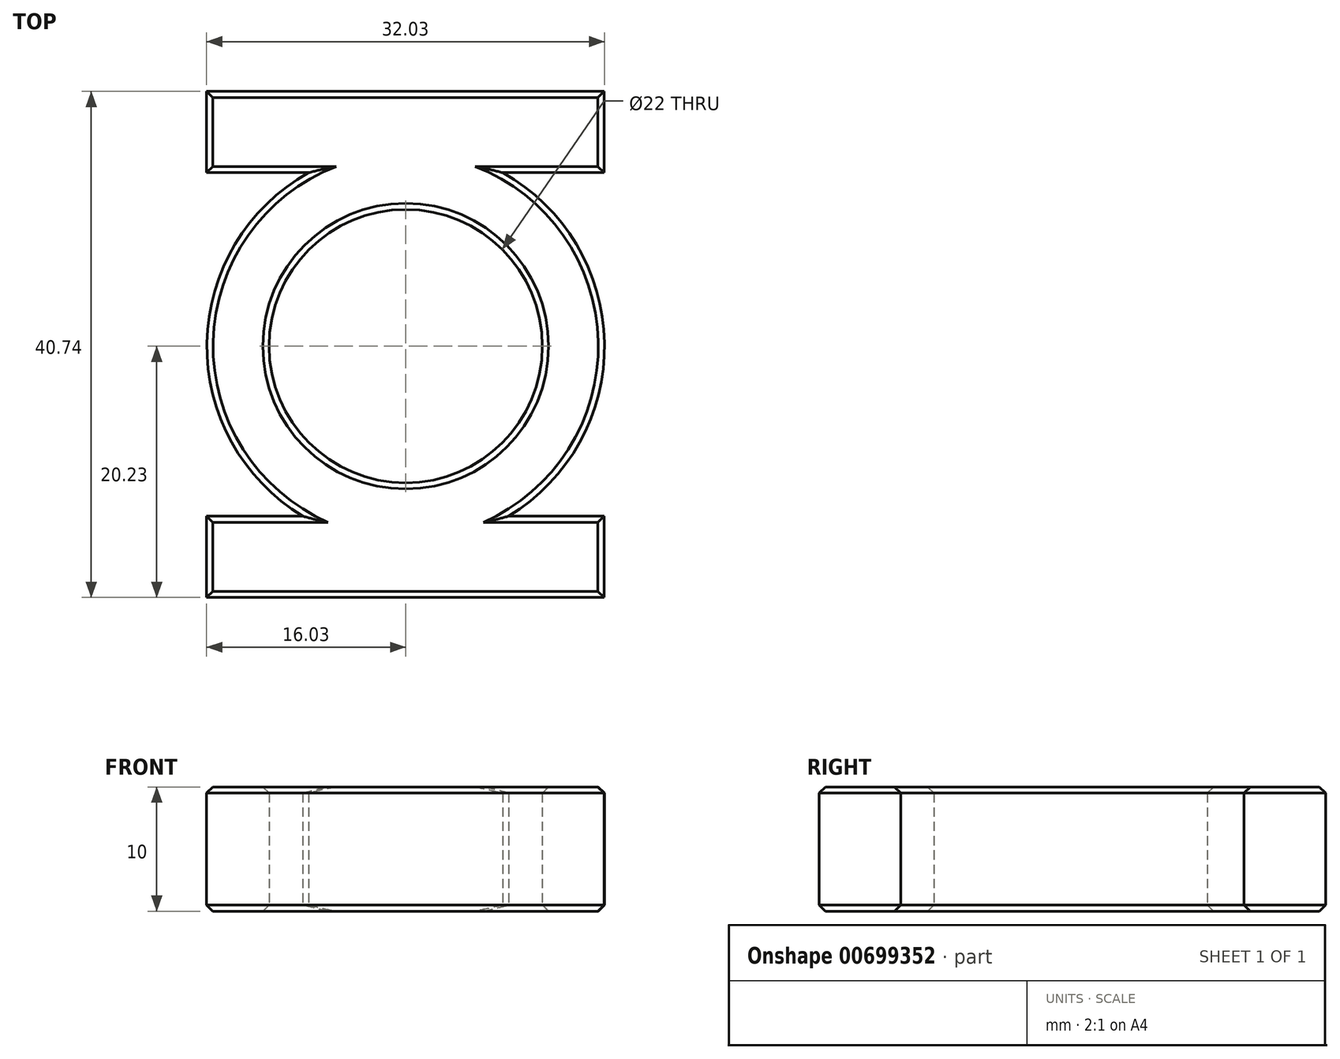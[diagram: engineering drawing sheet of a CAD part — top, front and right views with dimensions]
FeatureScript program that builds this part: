
annotation { "Feature Type Name" : "Feature", "Feature Type Description" : "" }
export const myFeature = defineFeature(function(context is Context, id is Id, definition is map)
    precondition{}
    {
        {
            var Q0;
            Q0=qCreatedBy(makeId("Top.planeOp"),FACE);
            var sketch = newSketch(context, id + "F0", { "sketchPlane" : qUnion([Q0])});
            skCircle(sketch, "E0", {"center": v(0, 0) * mm, "radius": 11 * mm});
            skArc(sketch, "E1", {"start": v(-7.82, 13.96) * mm, "mid": v(-16, 0.27) * mm, "end": v(-8.3, -13.68) * mm});
            skLineSegment(sketch, "E2", {"start": v(18.35, 0.14) * mm, "end": v(-21.03, 0.14) * mm, "construction": true});
            skLineSegment(sketch, "E3.bottom", {"start": v(-16.03, 20.5) * mm, "end": v(15.97, 20.5) * mm});
            skLineSegment(sketch, "E3.top", {"start": v(-16.03, 13.96) * mm, "end": v(-7.82, 13.96) * mm});
            skLineSegment(sketch, "E3.left", {"start": v(-16.03, 20.5) * mm, "end": v(-16.03, 13.96) * mm});
            skLineSegment(sketch, "E3.right", {"start": v(15.97, 20.5) * mm, "end": v(15.97, 13.96) * mm});
            skLineSegment(sketch, "E4.MirrorCS", {"start": v(-16.03, -20.23) * mm, "end": v(15.97, -20.23) * mm});
            skLineSegment(sketch, "E5.MirrorCS", {"start": v(15.97, -20.23) * mm, "end": v(15.97, -13.68) * mm});
            skLineSegment(sketch, "E6.MirrorCS", {"start": v(-16.03, -13.68) * mm, "end": v(-7.82, -13.68) * mm});
            skLineSegment(sketch, "E7.MirrorCS", {"start": v(-16.03, -13.68) * mm, "end": v(-8.3, -13.68) * mm});
            skLineSegment(sketch, "E8.MirrorCS", {"start": v(-16.03, -20.23) * mm, "end": v(-16.03, -13.68) * mm});
            skLineSegment(sketch, "E9", {"start": v(0, 21.7) * mm, "end": v(0, -22.05) * mm, "construction": true});
            skLineSegment(sketch, "E10.trimOffspring", {"start": v(7.82, 13.96) * mm, "end": v(15.97, 13.96) * mm});
            skLineSegment(sketch, "E11.MirrorCS", {"start": v(7.82, -13.68) * mm, "end": v(15.97, -13.68) * mm});
            skLineSegment(sketch, "E12.trimOffspring", {"start": v(8.3, -13.68) * mm, "end": v(15.97, -13.68) * mm});
            skArc(sketch, "E13.trimOffspring", {"start": v(8.3, -13.68) * mm, "mid": v(16, 0.27) * mm, "end": v(7.82, 13.96) * mm});
            skSolve(sketch);
        }
        {
            var Q0;
            Q0=makeQuery(id+"F0.imprint","IMPRINT",FACE,{"disambiguationData":[TD([[makeQuery(id+"F0.imprint","IMPRINT",EDGE,{"derivedFrom":sQuery(id+"F0.wireOp",EDGE,"E0")}),-1.0]])]});
            extrude(context, id + "F1", {"entities" : qUnion([Q0]), "endBound" : BoundingType.SYMMETRIC, "depth" : 10 * mm, "offsetDistance" : 25 * mm});
        }
        {
            var Q0;
            Q0=makeQuery(id+"F1.opExtrude","CAP_FACE",FACE,{"disambiguationData":[OSD([sQuery(id+"F0.wireOp",EDGE,"E0"),sQuery(id+"F0.wireOp",EDGE,"E1"),sQuery(id+"F0.wireOp",EDGE,"E3.bottom"),sQuery(id+"F0.wireOp",EDGE,"E3.top"),sQuery(id+"F0.wireOp",EDGE,"E3.left"),sQuery(id+"F0.wireOp",EDGE,"E3.right"),sQuery(id+"F0.wireOp",EDGE,"E5.MirrorCS"),sQuery(id+"F0.wireOp",EDGE,"E10.trimOffspring"),sQuery(id+"F0.wireOp",EDGE,"E4.MirrorCS"),sQuery(id+"F0.wireOp",EDGE,"E8.MirrorCS"),sQuery(id+"F0.wireOp",EDGE,"E6.MirrorCS"),sQuery(id+"F0.wireOp",EDGE,"E11.MirrorCS"),sQuery(id+"F0.wireOp",EDGE,"E13.trimOffspring")])],"isStart":false});
            chamfer(context, id + "F2", {"entities" : qUnion([Q0]), "chamferType" : ChamferType.OFFSET_ANGLE, "width" : .5 * mm, "oppositeDirection" : false, "angle" : 45 * degree, "tangentPropagation" : true});
        }
        {
            var Q0;
            Q0=makeQuery(id+"F1.opExtrude","CAP_FACE",FACE,{"disambiguationData":[OSD([sQuery(id+"F0.wireOp",EDGE,"E0"),sQuery(id+"F0.wireOp",EDGE,"E1"),sQuery(id+"F0.wireOp",EDGE,"E3.bottom"),sQuery(id+"F0.wireOp",EDGE,"E3.top"),sQuery(id+"F0.wireOp",EDGE,"E3.left"),sQuery(id+"F0.wireOp",EDGE,"E3.right"),sQuery(id+"F0.wireOp",EDGE,"E5.MirrorCS"),sQuery(id+"F0.wireOp",EDGE,"E10.trimOffspring"),sQuery(id+"F0.wireOp",EDGE,"E4.MirrorCS"),sQuery(id+"F0.wireOp",EDGE,"E8.MirrorCS"),sQuery(id+"F0.wireOp",EDGE,"E6.MirrorCS"),sQuery(id+"F0.wireOp",EDGE,"E11.MirrorCS"),sQuery(id+"F0.wireOp",EDGE,"E13.trimOffspring")])],"isStart":true});
            chamfer(context, id + "F3", {"entities" : qUnion([Q0]), "chamferType" : ChamferType.OFFSET_ANGLE, "width" : .5 * mm, "oppositeDirection" : true, "angle" : 45 * degree, "tangentPropagation" : true});
        }
    });
